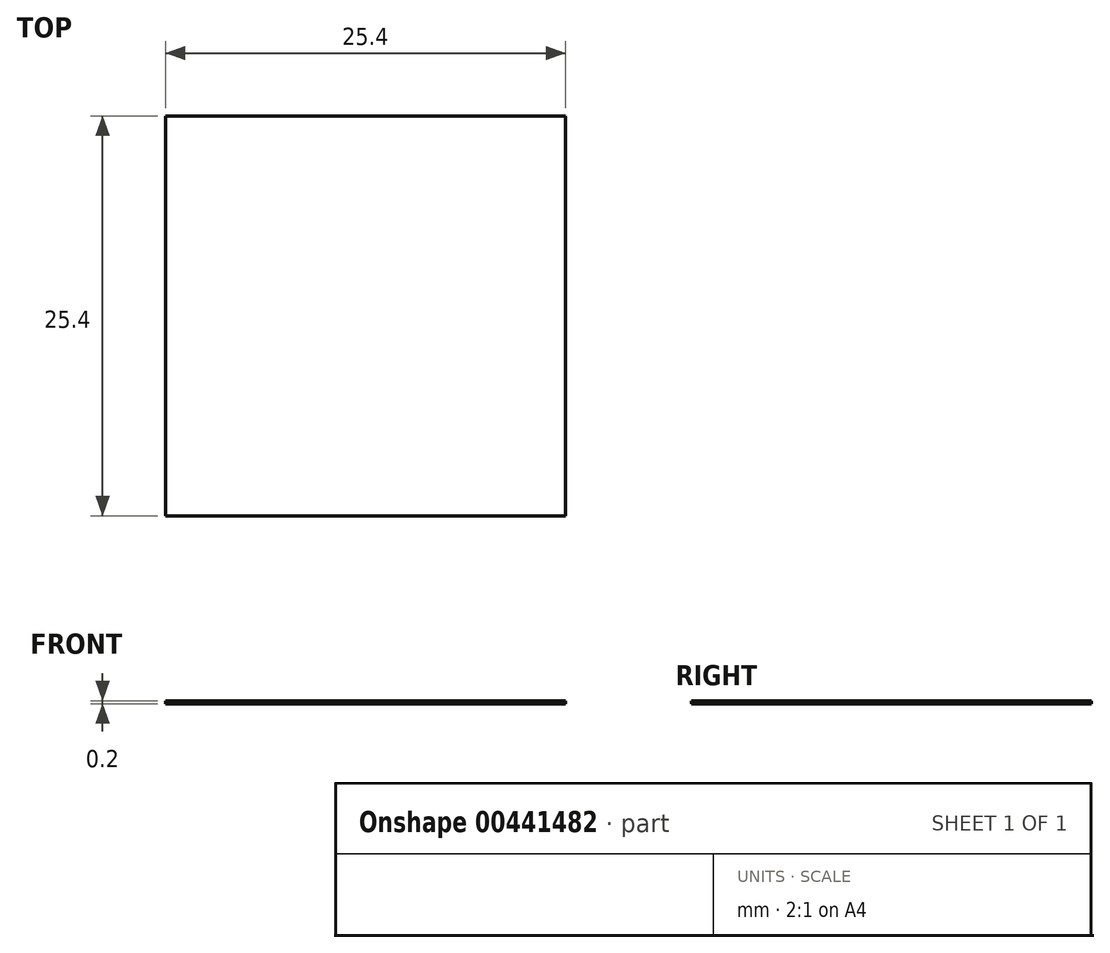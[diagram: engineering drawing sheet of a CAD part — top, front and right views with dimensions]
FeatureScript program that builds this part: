
annotation { "Feature Type Name" : "Feature", "Feature Type Description" : "" }
export const myFeature = defineFeature(function(context is Context, id is Id, definition is map)
    precondition{}
    {
        {
            var Q0;
            Q0=qCreatedBy(makeId("Top.planeOp"),FACE);
            var sketch = newSketch(context, id + "F0", { "sketchPlane" : qUnion([Q0])});
            skLineSegment(sketch, "E0.bottom", {"start": v(12.7, -12.7) * mm, "end": v(-12.7, -12.7) * mm});
            skLineSegment(sketch, "E0.top", {"start": v(12.7, 12.7) * mm, "end": v(-12.7, 12.7) * mm});
            skLineSegment(sketch, "E0.left", {"start": v(12.7, -12.7) * mm, "end": v(12.7, 12.7) * mm});
            skLineSegment(sketch, "E0.right", {"start": v(-12.7, -12.7) * mm, "end": v(-12.7, 12.7) * mm});
            skPoint(sketch, "E0.middle", {"position": v(0, 0) * mm});
            skSolve(sketch);
        }
        {
            var Q0;
            Q0 = qSketchRegion(id + "F0", true);
            extrude(context, id + "F1", {"entities" : qUnion([Q0]), "depth" : 0.2 * mm});
        }
    });
